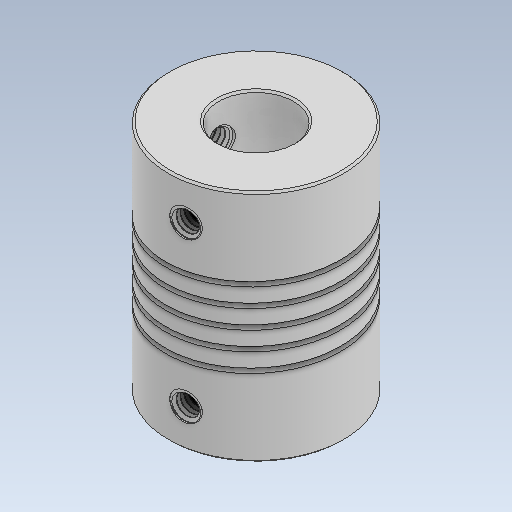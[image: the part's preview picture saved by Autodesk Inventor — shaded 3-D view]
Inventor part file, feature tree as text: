
AUTODESK INVENTOR PART (.ipt)
format: ipt  version: 2020 (Build 240168000, 168)  size: 2,975,232 bytes
history: native  units: mm
features: sketch x12, helix x5, thread x4, revolve x4, extrude x2, chamfer x2, hole x1, pattern_circular x1
ambient origin geometry x8: Origin, YZ Plane, XZ Plane, XY Plane, X Axis, Y Axis, Z Axis, Center Point
bodies: Solid1 (feature_tree), Solid2 (feature_tree), Solid3 (feature_tree), Solid4 (feature_tree), Solid5 (feature_tree)
feature tree (31):
  extrude  "Extrusion1"  Depth=25.0mm TaperAngle=0.0deg
  hole  "Hole1"  [1 undecoded]
  extrude  "Extrusion2"  Depth=10.0mm TaperAngle=0.0deg
  chamfer  "Chamfer1"  Distance=20.0mm
  pattern_circular  "Circular Pattern1"  [2 undecoded]
  thread  "Thread1"  [1 undecoded]
  thread  "Thread2"  [1 undecoded]
  thread  "Thread3"  [1 undecoded]
  thread  "Thread4"  [1 undecoded]
  revolve  "Revolution1"  [1 undecoded]
  helix  "Coil1"  [1 undecoded]
  revolve  "Revolution2"  [1 undecoded]
  helix  "Coil2"  [1 undecoded]
  revolve  "Revolution3"  [1 undecoded]
  helix  "Coil3"  [1 undecoded]
  revolve  "Revolution4"  [1 undecoded]
  helix  "Coil4"  [1 undecoded]
  helix  "Coil5"  [1 undecoded]
  chamfer  "Chamfer2"  Distance=0.5mm
  sketch  "Sketch1"  dims[d0=18.7mm d1=25.0mm d2=0.0mm]
  sketch  "Sketch2"  dims[d3=6.0mm d4=6.0mm d5=8.0mm d6=18.0mm d7=90.0deg d8=7.0mm d9=0.0mm d10=4.0mm]
  sketch  "Sketch3"  dims[d11=3.0mm d12=10.0mm d13=0.0mm d14=20.0mm d15=17.453293mm]
  sketch  "Sketch4"  dims[d18=0.15mm d19=2.0mm d20=45.0deg]
  sketch  "Sketch5"  dims[d21=5.2mm d22=0.0mm]
  sketch  "Sketch6"  dims[d23=5.2mm]
  sketch  "Sketch7"  dims[d24=0.0mm]
  sketch  "Sketch8"  dims[d25=6.7mm d26=0.0mm]
  sketch  "Sketch9"  dims[d27=6.7mm]
  sketch  "Sketch10"  dims[d28=0.0mm]
  sketch  "Sketch11"  dims[d29=9.599311mm d30=0.080042mm d31=0.080042mm]
  sketch  "Sketch12"  dims[d34=0.5mm d36=9.599311mm d38=0.0mm d39=0.5005mm d40=6.2mm d41=10.0mm d42=0.0mm d43=0.0mm d44=0.0mm d45=0.0mm d46=0.0mm d47=9.599311mm d48=0.080042mm d49=0.080042mm d52=0.5mm d54=9.599311mm d56=0.0mm d57=0.5005mm d58=6.2mm d59=10.0mm d60=0.0mm d61=0.0mm d62=0.0mm d63=0.0mm d64=0.0mm d65=9.599311mm d66=0.080042mm d67=0.080042mm d70=0.5mm d72=9.599311mm d74=0.0mm d75=0.5005mm d76=7.7mm d77=10.0mm d78=0.0mm d79=0.0mm d80=0.0mm d81=0.0mm d82=0.0mm d83=9.599311mm d84=0.080042mm d85=0.080042mm d88=0.5mm d90=9.599311mm d92=0.0mm d93=0.5005mm d94=7.7mm d95=10.0mm d96=0.0mm d97=0.0mm d98=0.0mm d99=0.0mm d100=0.0mm d101=0.5mm d102=7.0mm d103=7.0mm d104=2.0mm d105=9.9mm d106=50.0mm d107=0.0mm d108=90.0deg d109=90.0deg d110=0.0mm d111=0.0mm d112=0.2mm d113=2.0mm d114=45.0deg]
note: 16 required parameter values undecoded (feature->parameter linkage not recoverable at this tier; creation-order binding heuristic only, values carry confidence <= 0.55)